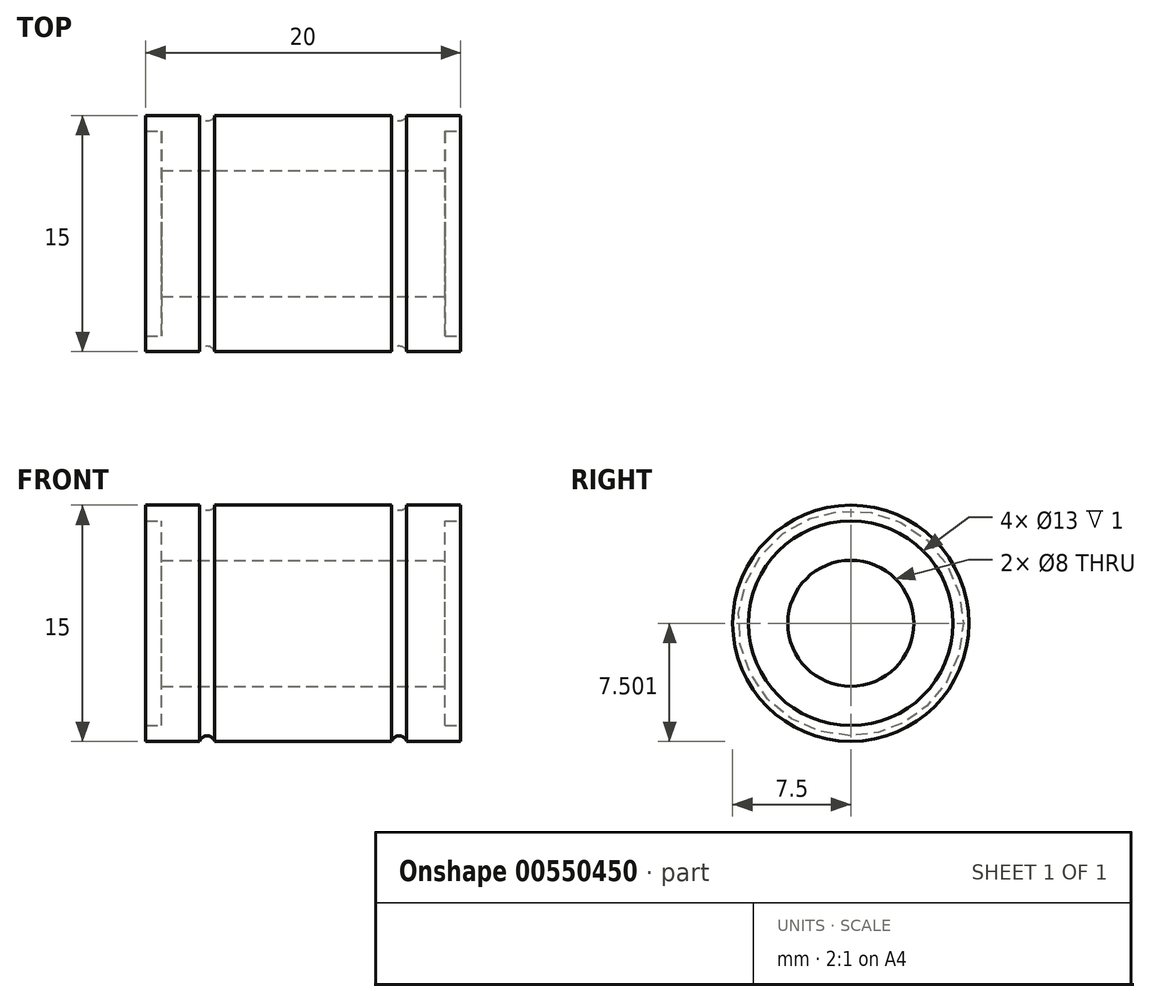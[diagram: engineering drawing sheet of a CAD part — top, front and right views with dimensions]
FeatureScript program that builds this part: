
annotation { "Feature Type Name" : "Feature", "Feature Type Description" : "" }
export const myFeature = defineFeature(function(context is Context, id is Id, definition is map)
    precondition{}
    {
        {
            var Q0;
            Q0=qCreatedBy(makeId("Front.planeOp"),FACE);
            var sketch = newSketch(context, id + "F0", { "sketchPlane" : qUnion([Q0])});
            skLineSegment(sketch, "E0", {"start": v(0, 10.93) * mm, "end": v(0, 9.93) * mm});
            skLineSegment(sketch, "E1", {"start": v(0, 9.93) * mm, "end": v(-1, 9.93) * mm});
            skArc(sketch, "E2.MirrorCS", {"start": v(-3.42, 10.93) * mm, "mid": v(-3.9, 10.58) * mm, "end": v(-4.38, 10.93) * mm});
            skLineSegment(sketch, "E3.trimOffspring", {"start": v(-3.42, 10.93) * mm, "end": v(0, 10.93) * mm});
            skLineSegment(sketch, "E4.trimOffspring", {"start": v(-20, 10.93) * mm, "end": v(-4.38, 10.93) * mm});
            skLineSegment(sketch, "E5", {"start": v(-1, 9.93) * mm, "end": v(-1, 7.43) * mm});
            skLineSegment(sketch, "E6", {"start": v(-1, 7.43) * mm, "end": v(-1.88, 7.43) * mm});
            skLineSegment(sketch, "E7", {"start": v(-1.88, 7.43) * mm, "end": v(-1.88, 3.43) * mm});
            skLineSegment(sketch, "E8", {"start": v(-1.88, 3.43) * mm, "end": v(-18.12, 3.43) * mm});
            skLineSegment(sketch, "E9.MirrorCS", {"start": v(-20, 10.93) * mm, "end": v(-20, 9.93) * mm});
            skLineSegment(sketch, "E10.MirrorCS", {"start": v(-20, 9.93) * mm, "end": v(-19, 9.93) * mm});
            skLineSegment(sketch, "E11.MirrorCS", {"start": v(-19, 9.93) * mm, "end": v(-19, 7.43) * mm});
            skArc(sketch, "E12.MirrorCS", {"start": v(-16.58, 10.93) * mm, "mid": v(-16.1, 10.58) * mm, "end": v(-15.62, 10.93) * mm});
            skLineSegment(sketch, "E13.MirrorCS", {"start": v(-19, 7.43) * mm, "end": v(-18.12, 7.43) * mm});
            skLineSegment(sketch, "E14.MirrorCS", {"start": v(-16.58, 10.93) * mm, "end": v(-20, 10.93) * mm});
            skLineSegment(sketch, "E15.MirrorCS", {"start": v(-18.12, 7.43) * mm, "end": v(-18.12, 3.43) * mm});
            skSolve(sketch);
        }
        {
            var Q0;
            Q0=makeQuery(id+"F0.imprint","IMPRINT",FACE,{"disambiguationData":[TD([[makeQuery(id+"F0.imprint","IMPRINT",EDGE,{"derivedFrom":sQuery(id+"F0.wireOp",EDGE,"3u3zcnXG-mea8-R9Tc-KXIq-p7IRRJW1LFod")}),-1.0]])]});
            var Q1;
            Q1=makeQuery(id+"F0.imprint","IMPRINT",FACE,{"disambiguationData":[TD([[makeQuery(id+"F0.imprint","IMPRINT",EDGE,{"derivedFrom":sQuery(id+"F0.wireOp",EDGE,"E0")}),-1.0]])]});
            var Q2;
            Q2=sQuery(id+"F0.wireOp",EDGE,"E8");
            revolve(context, id + "F1", {"entities" : qUnion([Q0, Q1]), "axis" : qUnion([Q2]), "revolveType" : RevolveType.FULL});
        }
        {
            var Q0;
            Q0=makeQuery(id+"F1.opRevolve","SWEPT_FACE",FACE,{"disambiguationData":[OSD([sQuery(id+"F0.wireOp",EDGE,"E15.MirrorCS")])]});
            extrude(context, id + "F2", {"entities" : qUnion([Q0]), "operationType" : NewBodyOperationType.REMOVE, "oppositeDirection" : true, "depth" : 25 * mm, "offsetDistance" : 25 * mm});
        }
    });
